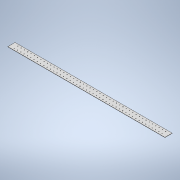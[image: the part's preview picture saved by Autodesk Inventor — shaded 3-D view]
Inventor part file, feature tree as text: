
AUTODESK INVENTOR PART (.ipt)
format: ipt  version: 2022 (Build 260153000, 153)  size: 238,080 bytes
history: native  units: mm
features: sheet_metal_op x1, sketch x1, other x1
ambient origin geometry x8: Origin, YZ Plane, XZ Plane, XY Plane, X Axis, Y Axis, Z Axis, Center Point
bodies: Body1 (feature_tree)
feature tree (3):
  sheet_metal_op  "Face2"
  sketch  "Sketch1"  dims[d0=44.0mm d1=956.0mm d2=11.0mm d3=28.0mm d4=3.35mm d5=460.0mm d7=20.0mm d8=20.0mm d10=22.0mm d14=1.5mm]
  other  "Plate2"
